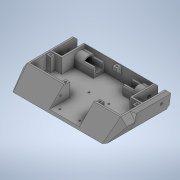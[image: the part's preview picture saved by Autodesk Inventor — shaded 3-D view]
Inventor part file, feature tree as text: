
AUTODESK INVENTOR PART (.ipt)
format: ipt  version: 2020 (Build 240168000, 168)  size: 713,728 bytes
history: native  units: mm
features: extrude x19, sketch x19, projected_geometry x13, chamfer x6, plane x4, mirror x3
ambient origin geometry x8: Origin, YZ Plane, XZ Plane, XY Plane, X Axis, Y Axis, Z Axis, Center Point
bodies: Solid1 (feature_tree)
feature tree (64):
  extrude  "Extrusion1"  Depth=120.0mm
  plane  "Work Plane2"
  extrude  "Extrusion6"  TaperAngle=0.0deg  [1 undecoded]
  chamfer  "Chamfer2"  Distance=83.204mm
  chamfer  "Chamfer3"  Distance=6.0mm Angle=45.0deg
  chamfer  "Chamfer4"  [1 undecoded]
  chamfer  "Chamfer6"  Distance=16.15mm
  extrude  "Extrusion9"  Depth=6.0mm
  extrude  "Extrusion10"  Depth=6.0mm TaperAngle=0.0deg
  extrude  "Extrusion11"  Depth=6.0mm
  extrude  "Extrusion12"  Depth=6.0mm TaperAngle=0.0deg
  mirror  "Mirror2"
  extrude  "WeaponMountSlot"  Depth=10.0mm TaperAngle=0.0deg
  chamfer  "Chamfer7"  Distance=37.4mm
  extrude  "Extrusion14"  Depth=55.8mm
  extrude  "Extrusion15"  Depth=2.0mm TaperAngle=45.0deg
  extrude  "Extrusion16"  Depth=8.0mm
  extrude  "Extrusion17"  Depth=25.5mm
  extrude  "WeaponMountHoles"  TaperAngle=0.0deg  [1 undecoded]
  extrude  "Extrusion19"  Depth=6.0mm
  extrude  "Extrusion20"  Depth=6.0mm
  extrude  "Extrusion21"  Depth=6.0mm
  mirror  "Mirror3"
  extrude  "Extrusion22"  Depth=6.0mm
  chamfer  "Chamfer8"  Distance=7.0mm
  plane  "Work Plane7"
  extrude  "Extrusion23"  TaperAngle=0.0deg  [1 undecoded]
  plane  "Work Plane9"
  extrude  "Extrusion27"  Depth=6.0mm
  plane  "Work Plane11"
  extrude  "Extrusion29"  Depth=6.0mm
  mirror  "Mirror5"
  sketch  "Sketch1"  dims[d0=180.0mm d1=120.0mm]
  sketch  "Sketch7"  dims[d2=30.0mm d3=0.0mm]
  projected_geometry  "Projected Loop3"
  sketch  "Sketch11"  dims[d10=45.0deg d18=83.204mm d19=0.0mm]
  projected_geometry  "Projected Loop4"
  sketch  "Sketch12"  dims[d27=3.0mm d28=6.0mm d29=45.0deg]
  projected_geometry  "Projected Loop8"
  sketch  "Sketch16"  dims[d30=24.0mm]
  sketch  "Sketch17"  dims[d31=3.0mm]
  sketch  "Sketch18"  dims[d32=45.0deg]
  sketch  "Sketch19"  dims[d33=3.0mm]
  sketch  "Sketch20"  dims[d34=6.0mm]
  projected_geometry  "Projected Loop9"
  projected_geometry  "Projected Loop10"
  projected_geometry  "Projected Loop11"
  projected_geometry  "Projected Loop12"
  sketch  "Sketch21"  dims[d35=45.0deg]
  sketch  "Sketch22"  dims[d39=24.0mm]
  sketch  "Sketch23"  dims[d40=3.0mm]
  sketch  "Sketch24"  dims[d41=45.0deg]
  sketch  "Sketch25"  dims[d45=17.7mm]
  sketch  "Sketch26"  dims[d46=46.15mm d47=0.0mm d48=0.0mm]
  projected_geometry  "Projected Loop13"
  sketch  "Sketch27"  dims[d52=27.0mm]
  projected_geometry  "Projected Loop14"
  sketch  "Sketch31"  dims[d53=0.0mm]
  projected_geometry  "Projected Loop20"
  projected_geometry  "Projected Loop21"
  sketch  "Sketch37"  dims[d58=6.0mm]
  sketch  "Sketch39"  dims[d64=6.5mm d65=16.15mm d66=15.0mm d67=157.438mm d68=0.0mm d69=4.5mm d70=173.156mm d71=0.0mm d72=10.0mm d73=0.0mm d75=37.4mm d76=55.8mm d77=5.0mm d78=2.0mm d79=45.0deg d80=8.0mm d81=25.5mm d82=0.0mm d83=3.75mm d84=3.75mm d85=3.75mm d86=3.75mm d87=7.0mm d88=0.0mm d90=6.0mm d91=4.0mm d92=15.0mm d93=23.0mm d94=7.0mm d95=0.0mm d96=4.0mm d97=15.0mm d98=23.0mm d99=7.0mm d100=0.0mm d101=3.0mm d102=60.0mm d103=3.1mm d104=3.1mm d105=3.1mm d106=3.1mm d107=10.0mm d108=9.4mm d109=9.4mm d110=64.0mm d111=64.0mm d112=9.4mm d113=9.4mm d114=10.0mm d115=27.0mm d116=0.0mm d117=6.1mm d118=0.0mm d119=-7.853982mm d120=16.3mm d121=16.15mm d122=15.0mm d123=2.0mm d124=20.3mm d125=17.0mm d126=0.0mm d127=15.5mm d128=12.2mm d129=19.0mm d130=0.0mm d131=45.0deg d133=19.0mm d134=0.0mm d135=8.0mm d137=6.1mm d138=3.0mm d139=3.0mm d140=4.0mm d141=2.0mm d142=45.0deg d144=10.0mm d145=0.0mm d148=6.0mm d149=-72.0mm d156=5.0mm d157=0.0mm d161=5.0mm d162=0.0mm d164=8.726646mm d165=-7.853982mm]
  projected_geometry  "Project Cut Edges3"
  projected_geometry  "Project Cut Edges4"
note: 4 required parameter values undecoded (feature->parameter linkage not recoverable at this tier; creation-order binding heuristic only, values carry confidence <= 0.55)
